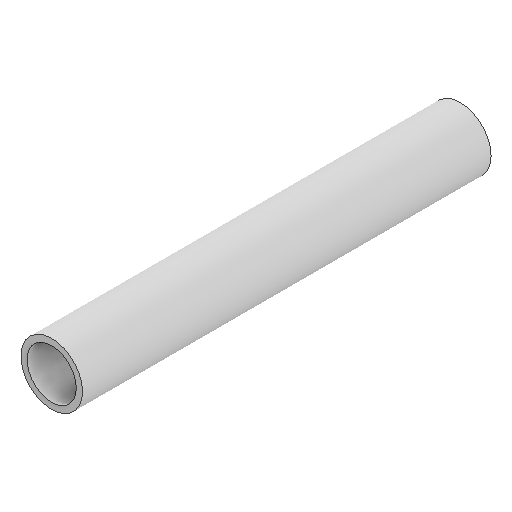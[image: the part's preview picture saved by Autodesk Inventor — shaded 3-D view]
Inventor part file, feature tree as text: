
AUTODESK INVENTOR PART (.ipt)
format: ipt  version: 2025.1 (Build 291241000, 241)  size: 91,648 bytes
history: native  units: mm
features: other x1, extrude x1, sketch x1
ambient origin geometry x8: Origin, YZ Plane, XZ Plane, XY Plane, X Axis, Y Axis, Z Axis, Center Point
bodies: Body1 (feature_tree)
feature tree (3):
  other  "Bryła1"
  extrude  "Wyciągnięcie proste1"  Depth=4.0mm
  sketch  "Szkic1"
